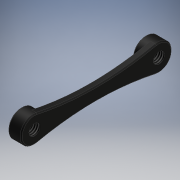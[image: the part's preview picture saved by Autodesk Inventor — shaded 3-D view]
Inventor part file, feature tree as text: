
AUTODESK INVENTOR PART (.ipt)
format: ipt  version: 2018 (Build 220112000, 112)  size: 147,968 bytes
history: native  units: mm
features: sketch x3, projected_geometry x3, extrude x2, hole x1, chamfer x1
ambient origin geometry x8: Origin, YZ Plane, XZ Plane, XY Plane, X Axis, Y Axis, Z Axis, Center Point
bodies: Solid1 (feature_tree)
feature tree (10):
  extrude  "Extrusion1"  Depth=28.0mm
  extrude  "Extrusion2"  Depth=3.0mm
  hole  "Hole1"  [1 undecoded]
  chamfer  "Chamfer1"  [1 undecoded]
  sketch  "Sketch1"  dims[d0=6.0mm d1=28.0mm]
  sketch  "Sketch2"  dims[d2=3.0mm d3=0.0mm d4=3.0mm]
  projected_geometry  "Projected Loop1"
  projected_geometry  "Projected Loop2"
  sketch  "Sketch3"  dims[d5=1.5mm d6=0.0mm d7=2.459mm d8=6.0mm d9=4.0mm d10=2.0mm d11=90.0deg d12=8.0mm d13=20.594885mm d14=0.25mm d15=2.0mm d16=45.0deg]
  projected_geometry  "Projected Loop3"
note: 2 required parameter values undecoded (feature->parameter linkage not recoverable at this tier; creation-order binding heuristic only, values carry confidence <= 0.55)
